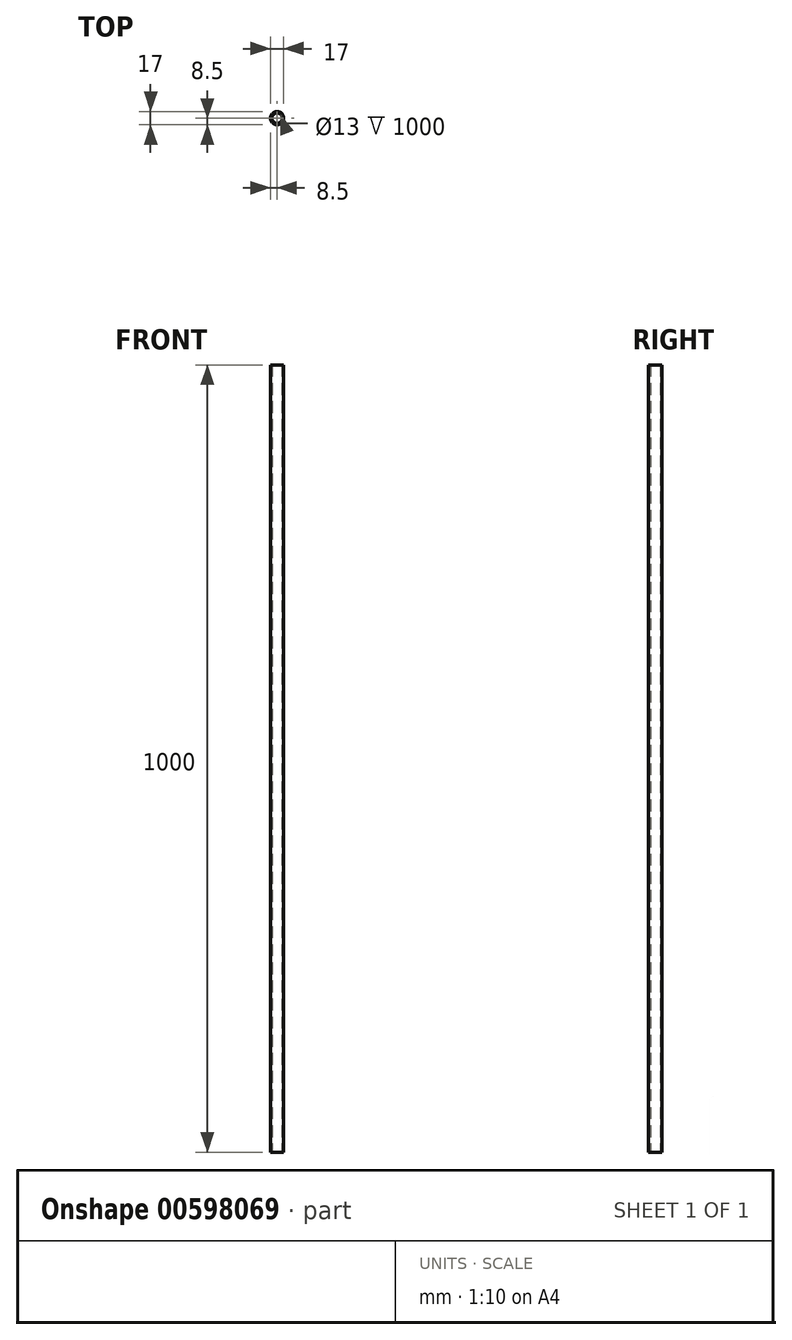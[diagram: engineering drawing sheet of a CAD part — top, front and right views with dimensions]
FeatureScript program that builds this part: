
annotation { "Feature Type Name" : "Feature", "Feature Type Description" : "" }
export const myFeature = defineFeature(function(context is Context, id is Id, definition is map)
    precondition{}
    {
        {
            var Q0;
            Q0=qCreatedBy(makeId("Top.planeOp"),FACE);
            var sketch = newSketch(context, id + "F0", { "sketchPlane" : qUnion([Q0])});
            skCircle(sketch, "E0", {"center": v(0, 0) * mm, "radius": 8.5 * mm});
            skCircle(sketch, "E1", {"center": v(0, 0) * mm, "radius": 6.5 * mm});
            skSolve(sketch);
        }
        {
            var Q0;
            Q0=makeQuery(id+"F0.imprint","IMPRINT",FACE,{"disambiguationData":[TD([[makeQuery(id+"F0.imprint","IMPRINT",EDGE,{"derivedFrom":sQuery(id+"F0.wireOp",EDGE,"E0")}),1.0]])]});
            extrude(context, id + "F1", {"entities" : qUnion([Q0]), "depth" : 1000 * mm, "offsetDistance" : 25 * mm});
        }
    });
